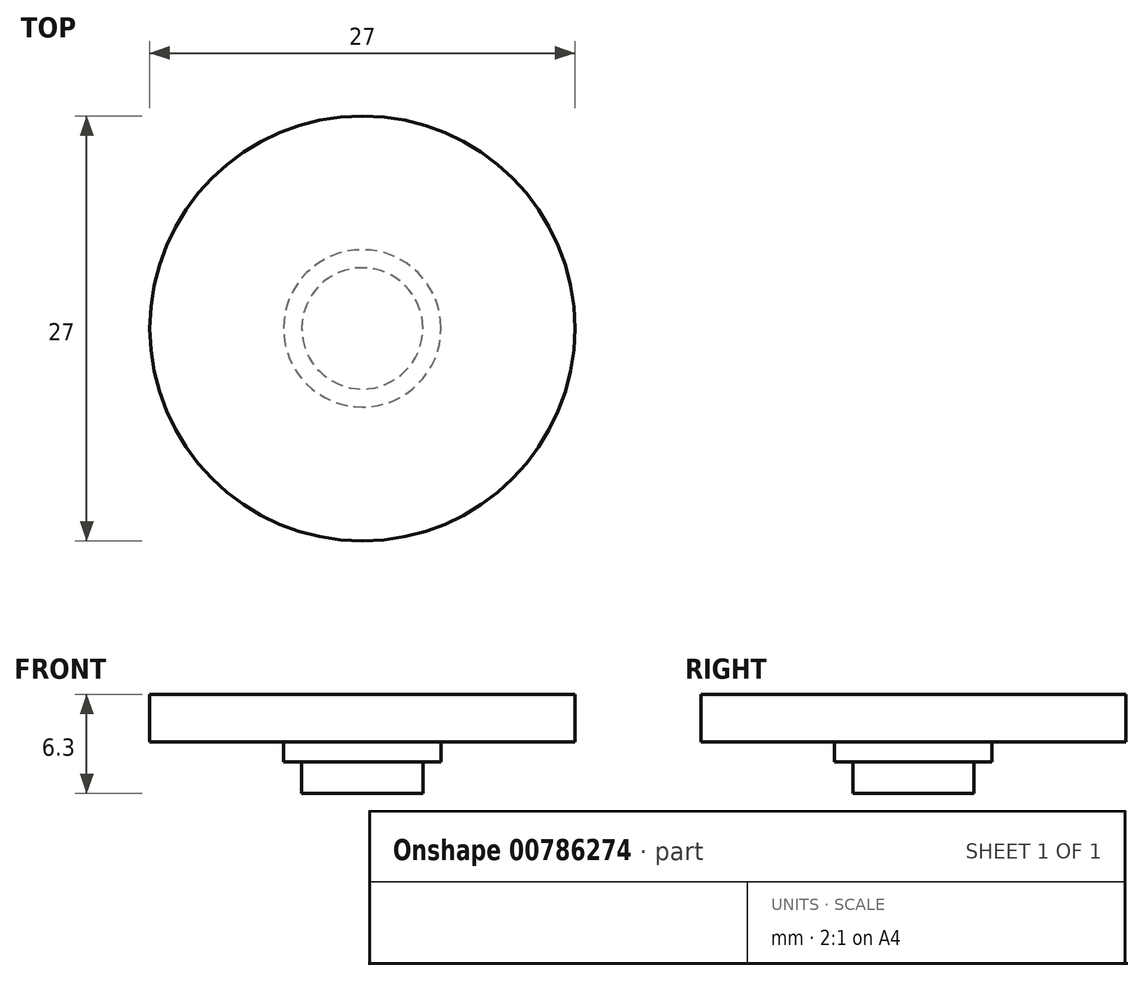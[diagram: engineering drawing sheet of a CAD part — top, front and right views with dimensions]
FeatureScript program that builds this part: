
annotation { "Feature Type Name" : "Feature", "Feature Type Description" : "" }
export const myFeature = defineFeature(function(context is Context, id is Id, definition is map)
    precondition{}
    {
        {
            var Q0;
            Q0=qCreatedBy(makeId("Top.planeOp"),FACE);
            var sketch = newSketch(context, id + "F0", { "sketchPlane" : qUnion([Q0])});
            skCircle(sketch, "E0", {"center": v(0, 0) * mm, "radius": 13.5 * mm});
            skSolve(sketch);
        }
        {
            var Q0;
            Q0 = qSketchRegion(id + "F0", true);
            extrude(context, id + "F1", {"entities" : qUnion([Q0]), "depth" : 3 * mm, "offsetDistance" : 25 * mm});
        }
        {
            var Q0;
            Q0=qCreatedBy(makeId("Top.planeOp"),FACE);
            var sketch = newSketch(context, id + "F2", { "sketchPlane" : qUnion([Q0])});
            skCircle(sketch, "E1", {"center": v(0, 0) * mm, "radius": 3.85 * mm});
            skCircle(sketch, "E2", {"center": v(0, 0) * mm, "radius": 5 * mm});
            skSolve(sketch);
        }
        {
            var Q0;
            Q0=makeQuery(id+"F2.imprint","IMPRINT",FACE,{"disambiguationData":[TD([[makeQuery(id+"F2.imprint","IMPRINT",EDGE,{"derivedFrom":sQuery(id+"F2.wireOp",EDGE,"E1")}),-1.0]])]});
            extrude(context, id + "F3", {"entities" : qUnion([Q0]), "operationType" : NewBodyOperationType.ADD, "oppositeDirection" : true, "depth" : 1.3 * mm, "offsetDistance" : 25 * mm});
        }
        {
            var Q0;
            Q0=makeQuery(id+"F3.boolean.opBoolean","SPLIT",FACE,{"disambiguationData":[TD([makeQuery(id+"F3.opExtrude","SWEPT_FACE",FACE,{"disambiguationData":[OSD([sQuery(id+"F2.wireOp",EDGE,"E1")])]})])],"derivedFrom":makeQuery(id+"F1.opExtrude","CAP_FACE",FACE,{"disambiguationData":[OSD([sQuery(id+"F0.wireOp",EDGE,"E0")])],"isStart":true})});
            extrude(context, id + "F4", {"entities" : qUnion([Q0]), "operationType" : NewBodyOperationType.ADD, "depth" : 3.3 * mm, "offsetDistance" : 25 * mm});
        }
    });
